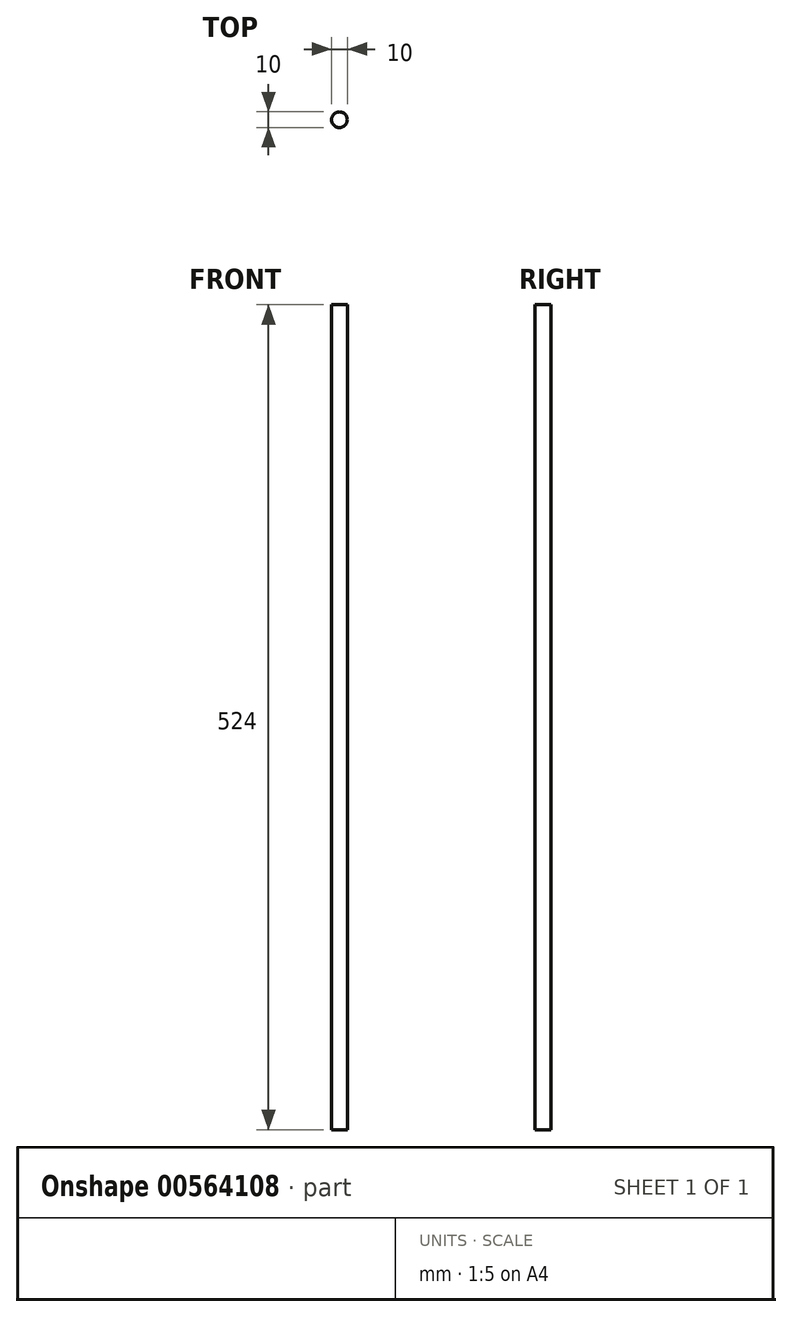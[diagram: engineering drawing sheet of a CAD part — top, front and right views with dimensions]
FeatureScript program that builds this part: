
annotation { "Feature Type Name" : "Feature", "Feature Type Description" : "" }
export const myFeature = defineFeature(function(context is Context, id is Id, definition is map)
    precondition{}
    {
        {
            var Q0;
            Q0=qCreatedBy(makeId("Top.planeOp"),FACE);
            var sketch = newSketch(context, id + "F0", { "sketchPlane" : qUnion([Q0])});
            skCircle(sketch, "E0", {"center": v(0, 0) * mm, "radius": 5 * mm});
            skSolve(sketch);
        }
        {
            var Q0;
            Q0=makeQuery(id+"F0.imprint","IMPRINT",FACE,{"disambiguationData":[TD([[makeQuery(id+"F0.imprint","IMPRINT",EDGE,{"derivedFrom":sQuery(id+"F0.wireOp",EDGE,"E0")}),1.0]])]});
            extrude(context, id + "F1", {"entities" : qUnion([Q0]), "depth" : 524 * mm, "offsetDistance" : 25 * mm});
        }
    });
